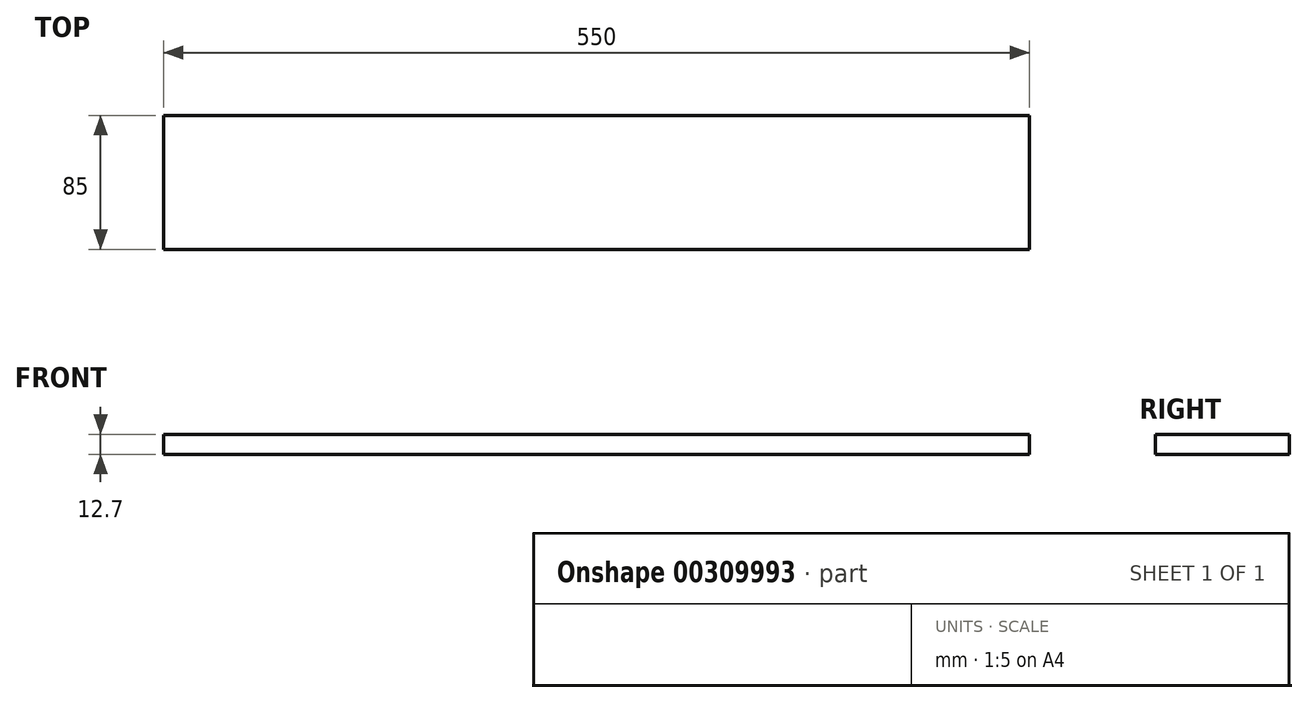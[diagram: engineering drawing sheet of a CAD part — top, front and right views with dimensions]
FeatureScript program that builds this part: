
annotation { "Feature Type Name" : "Feature", "Feature Type Description" : "" }
export const myFeature = defineFeature(function(context is Context, id is Id, definition is map)
    precondition{}
    {
        {
            var Q0;
            Q0=qCreatedBy(makeId("Top.planeOp"),FACE);
            var sketch = newSketch(context, id + "F0", { "sketchPlane" : qUnion([Q0])});
            skLineSegment(sketch, "E0.bottom", {"start": v(-275, 42.5) * mm, "end": v(275, 42.5) * mm});
            skLineSegment(sketch, "E0.top", {"start": v(-275, -42.5) * mm, "end": v(275, -42.5) * mm});
            skLineSegment(sketch, "E0.left", {"start": v(-275, 42.5) * mm, "end": v(-275, -42.5) * mm});
            skLineSegment(sketch, "E0.right", {"start": v(275, 42.5) * mm, "end": v(275, -42.5) * mm});
            skLineSegment(sketch, "E1", {"start": v(-275, 42.5) * mm, "end": v(275, -42.5) * mm, "construction": true});
            skSolve(sketch);
        }
        {
            var Q0;
            Q0 = qSketchRegion(id + "F0", true);
            extrude(context, id + "F1", {"entities" : qUnion([Q0]), "depth" : 12.7 * mm});
        }
    });
